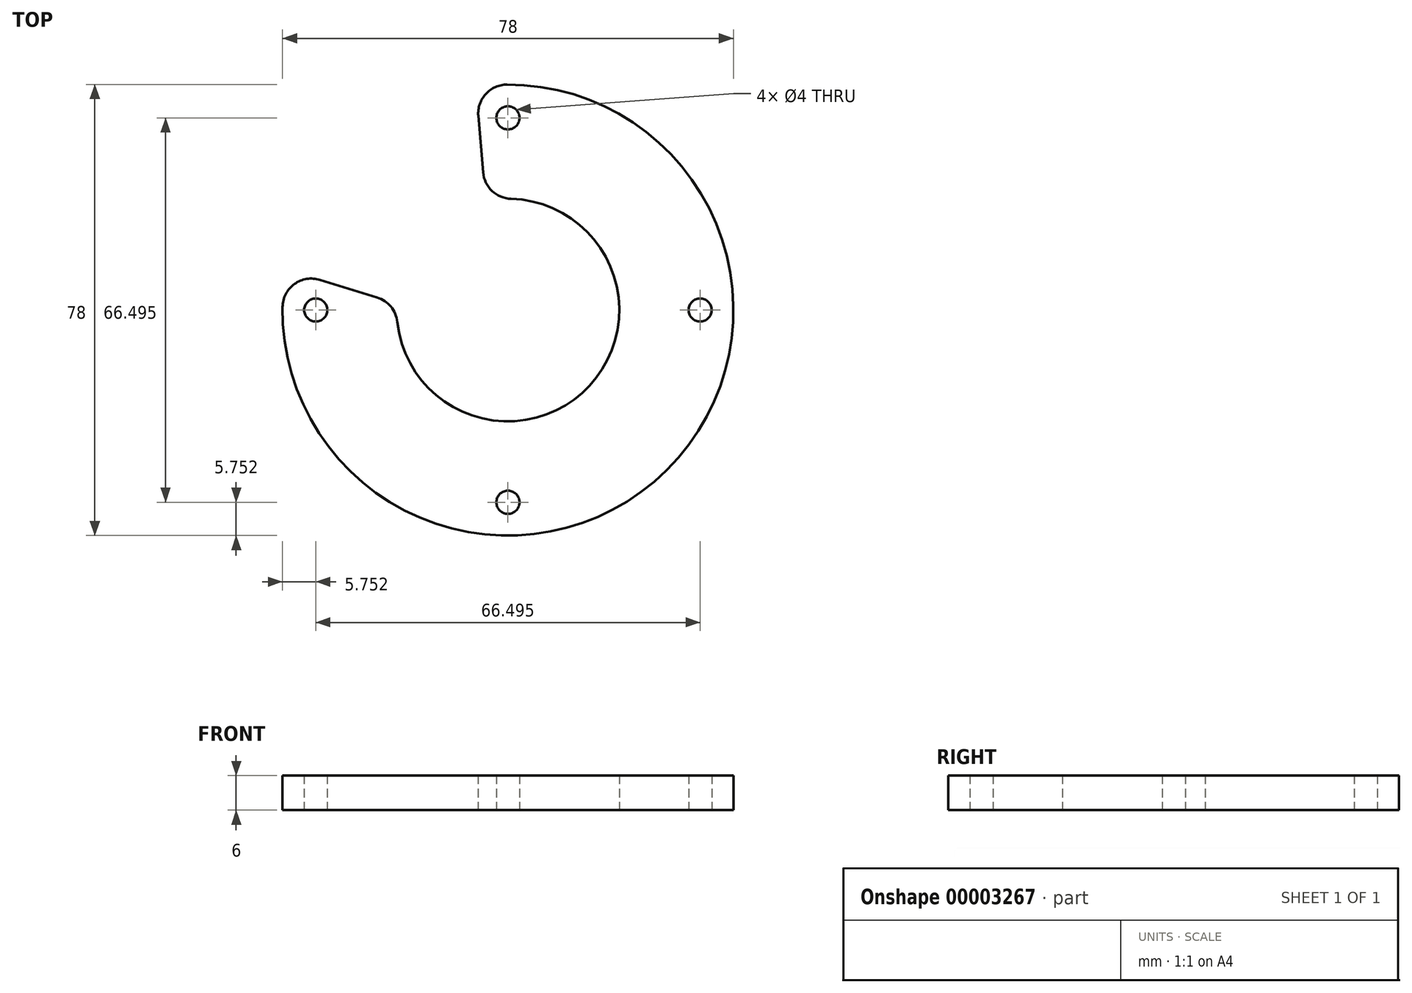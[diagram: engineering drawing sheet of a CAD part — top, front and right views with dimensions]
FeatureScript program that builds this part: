
annotation { "Feature Type Name" : "Feature", "Feature Type Description" : "" }
export const myFeature = defineFeature(function(context is Context, id is Id, definition is map)
    precondition{}
    {
        {
            var Q0;
            Q0=qCreatedBy(makeId("Top.planeOp"),FACE);
            var sketch = newSketch(context, id + "F0", { "sketchPlane" : qUnion([Q0])});
            skCircle(sketch, "E0", {"center": v(-33.25, 0) * mm, "radius": 2 * mm});
            skCircle(sketch, "E1", {"center": v(0, 33.25) * mm, "radius": 2 * mm});
            skCircle(sketch, "E2", {"center": v(33.25, 0) * mm, "radius": 2 * mm});
            skCircle(sketch, "E3", {"center": v(0, -33.25) * mm, "radius": 2 * mm});
            skArc(sketch, "E4", {"start": v(-39, 0.51) * mm, "mid": v(27.45, -27.7) * mm, "end": v(-0.16, 39) * mm});
            skArc(sketch, "E5", {"start": v(-19.14, -2.06) * mm, "mid": v(14.14, -13.06) * mm, "end": v(0.54, 19.24) * mm});
            skLineSegment(sketch, "E6", {"start": v(-32.52, 5.23) * mm, "end": v(-22.64, 2.18) * mm});
            skLineSegment(sketch, "E7", {"start": v(-5.12, 33.58) * mm, "end": v(-4.3, 23.82) * mm});
            skPoint(sketch, "E8.visualSharp", {"position": v(-38.36, 7.03) * mm});
            skArc(sketch, "E8.filletArc", {"start": v(-32.52, 5.23) * mm, "mid": v(-36.94, 4.49) * mm, "end": v(-39, 0.51) * mm});
            skPoint(sketch, "E9.visualSharp", {"position": v(16.52, -9.89) * mm});
            skArc(sketch, "E9.filletArc", {"start": v(-19.14, -2.06) * mm, "mid": v(-20.25, 0.58) * mm, "end": v(-22.64, 2.18) * mm});
            skPoint(sketch, "E10.visualSharp", {"position": v(-0.67, -19.24) * mm});
            skArc(sketch, "E10.filletArc", {"start": v(-4.3, 23.82) * mm, "mid": v(-2.75, 20.6) * mm, "end": v(0.54, 19.24) * mm});
            skPoint(sketch, "E11.visualSharp", {"position": v(-5.55, 38.6) * mm});
            skArc(sketch, "E11.filletArc", {"start": v(-0.16, 39) * mm, "mid": v(-3.83, 37.38) * mm, "end": v(-5.12, 33.58) * mm});
            skSolve(sketch);
        }
        {
            var Q0;
            Q0 = qSketchRegion(id + "F0", true);
            extrude(context, id + "F1", {"entities" : qUnion([Q0]), "depth" : 6 * mm});
        }
    });
